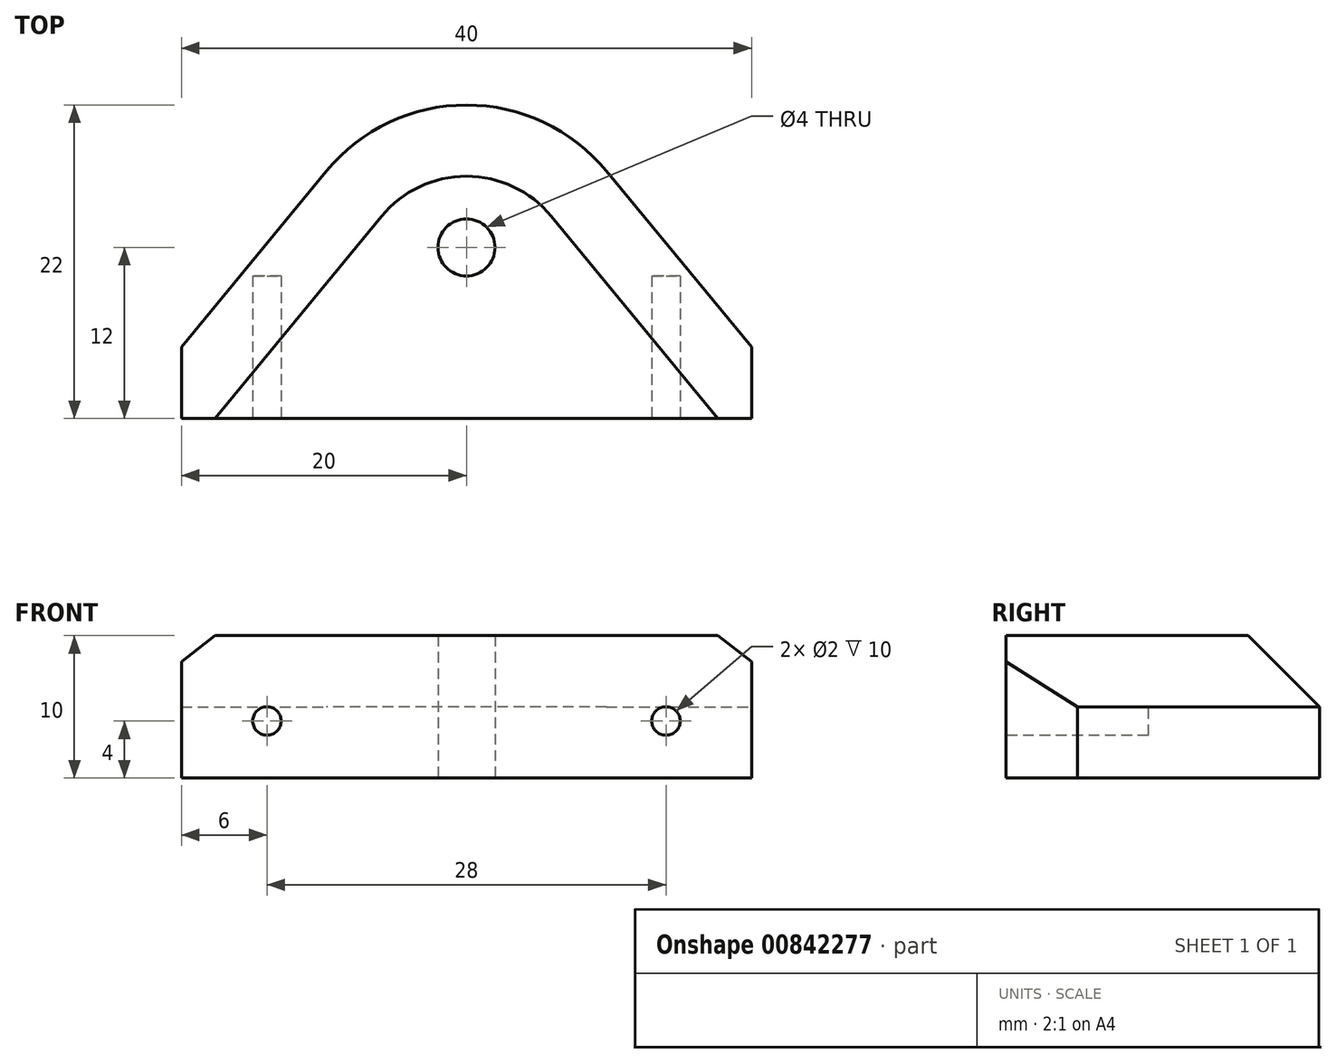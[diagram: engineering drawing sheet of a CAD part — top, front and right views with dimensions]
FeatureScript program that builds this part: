
annotation { "Feature Type Name" : "Feature", "Feature Type Description" : "" }
export const myFeature = defineFeature(function(context is Context, id is Id, definition is map)
    precondition{}
    {
        {
            var Q0;
            Q0=qCreatedBy(makeId("Top.planeOp"),FACE);
            var sketch = newSketch(context, id + "F0", { "sketchPlane" : qUnion([Q0])});
            skLineSegment(sketch, "E0.bottom", {"start": v(-20, 10) * mm, "end": v(20, 10) * mm});
            skLineSegment(sketch, "E0.top", {"start": v(-20, -12) * mm, "end": v(20, -12) * mm});
            skLineSegment(sketch, "E0.left", {"start": v(-20, 10) * mm, "end": v(-20, -12) * mm});
            skLineSegment(sketch, "E0.right", {"start": v(20, 10) * mm, "end": v(20, -12) * mm});
            skLineSegment(sketch, "E1.top", {"start": v(-20, -7) * mm, "end": v(20, -7) * mm});
            skLineSegment(sketch, "E1.left", {"start": v(-20, -12) * mm, "end": v(-20, -7) * mm});
            skLineSegment(sketch, "E1.right", {"start": v(20, -12) * mm, "end": v(20, -7) * mm});
            skCircle(sketch, "E2", {"center": v(0, 0) * mm, "radius": 2 * mm});
            skLineSegment(sketch, "E3", {"start": v(-20, -7) * mm, "end": v(-6, 10) * mm});
            skLineSegment(sketch, "E4", {"start": v(6, 10) * mm, "end": v(20, -7) * mm});
            skArc(sketch, "E5", {"start": v(9.81, 5.37) * mm, "mid": v(0, 10) * mm, "end": v(-9.81, 5.37) * mm});
            skSolve(sketch);
        }
        {
            var Q0;
            {var subQ0=sQuery(id+"F0.wireOp",EDGE,"E0.top");Q0=makeQuery(id+"F0.imprint","IMPRINT",FACE,{"disambiguationData":[TD([[makeQuery(id+"F0.imprint","IMPRINT",EDGE,{"derivedFrom":subQ0}),1.0]])]});}
            var Q1;
            {var subQ1=sQuery(id+"F0.wireOp",EDGE,"E1.top");Q1=makeQuery(id+"F0.imprint","IMPRINT",FACE,{"disambiguationData":[TD([[makeQuery(id+"F0.imprint","IMPRINT",EDGE,{"derivedFrom":subQ1}),1.0]])]});}
            extrude(context, id + "F1", {"entities" : qUnion([Q0, Q1]), "depth" : 10 * mm, "offsetDistance" : 25 * mm});
        }
        {
            var Q0;
            Q0=makeQuery(id+"F1.opExtrude","SWEPT_FACE",FACE,{"disambiguationData":[OSD([sQuery(id+"F0.wireOp",EDGE,"E0.top")])]});
            var sketch = newSketch(context, id + "F2", { "sketchPlane" : qUnion([Q0])});
            skCircle(sketch, "E6", {"center": v(-14, 4) * mm, "radius": 1 * mm});
            skCircle(sketch, "E7", {"center": v(14, 4) * mm, "radius": 1 * mm});
            skSolve(sketch);
        }
        {
            var Q0;
            Q0 = qSketchRegion(id + "F2", true);
            extrude(context, id + "F3", {"entities" : qUnion([Q0]), "operationType" : NewBodyOperationType.REMOVE, "oppositeDirection" : true, "depth" : 10 * mm, "offsetDistance" : 25 * mm});
        }
        {
            var Q0;
            Q0=makeQuery(id+"F1.opExtrude","CAP_EDGE",EDGE,{"disambiguationData":[OSD([sQuery(id+"F0.wireOp",EDGE,"E4")])],"isStart":false});
            chamfer(context, id + "F4", {"entities" : qUnion([Q0]), "width" : 5 * mm, "tangentPropagation" : true});
        }
    });
